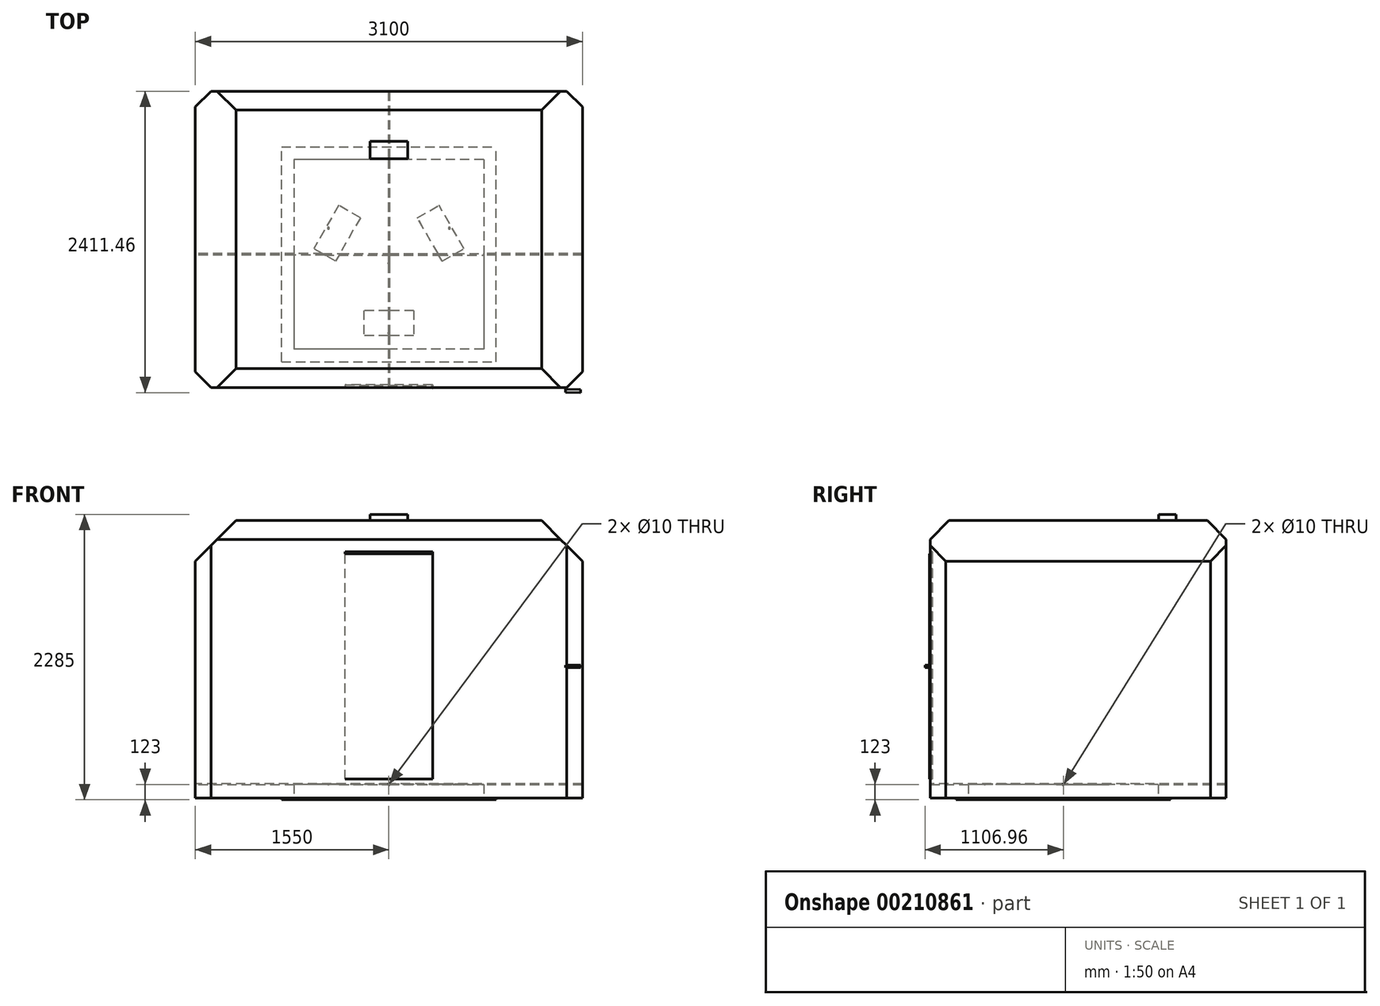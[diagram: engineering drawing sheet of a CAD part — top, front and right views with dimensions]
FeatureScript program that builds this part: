
annotation { "Feature Type Name" : "Feature", "Feature Type Description" : "" }
export const myFeature = defineFeature(function(context is Context, id is Id, definition is map)
    precondition{}
    {
        {
            var Q0;
            Q0=qCreatedBy(makeId("Front.planeOp"),FACE);
            var sketch = newSketch(context, id + "F0", { "sketchPlane" : qUnion([Q0])});
            skLineSegment(sketch, "E0.bottom", {"start": v(1550, -1110) * mm, "end": v(-1550, -1110) * mm});
            skLineSegment(sketch, "E0.top", {"start": v(1550, 1110) * mm, "end": v(-1550, 1110) * mm});
            skLineSegment(sketch, "E0.left", {"start": v(1550, -1110) * mm, "end": v(1550, 1110) * mm});
            skLineSegment(sketch, "E0.right", {"start": v(-1550, -1110) * mm, "end": v(-1550, 1110) * mm});
            skPoint(sketch, "E0.middle", {"position": v(0, 0) * mm});
            skSolve(sketch);
        }
        {
            var Q0;
            Q0=qSketchRegion(id+"F0",true);
            extrude(context, id + "F1", {"entities" : qUnion([Q0]), "depth" : 2370 * mm});
        }
        {
            var Q0;
            Q0=makeQuery(id+"F1.opExtrude","SWEPT_EDGE",EDGE,{"disambiguationData":[OSD([sQuery(id+"F0.wireOp",EDGE,"E0.top"),sQuery(id+"F0.wireOp",EDGE,"E0.right")])]});
            chamfer(context, id + "F2", {"entities" : qUnion([Q0]), "width" : 325 * mm, "tangentPropagation" : true});
        }
        {
            var Q0;
            Q0=makeQuery(id+"F1.opExtrude","SWEPT_EDGE",EDGE,{"disambiguationData":[OSD([sQuery(id+"F0.wireOp",EDGE,"E0.top"),sQuery(id+"F0.wireOp",EDGE,"E0.left")])]});
            chamfer(context, id + "F3", {"entities" : qUnion([Q0]), "width" : 325 * mm, "tangentPropagation" : true});
        }
        {
            var Q0;
            Q0=makeQuery(id+"F1.opExtrude","CAP_EDGE",EDGE,{"disambiguationData":[OSD([sQuery(id+"F0.wireOp",EDGE,"E0.left")])],"isStart":false});
            chamfer(context, id + "F4", {"entities" : qUnion([Q0]), "width" : 125 * mm, "tangentPropagation" : true});
        }
        {
            var Q0;
            Q0=makeQuery(id+"F1.opExtrude","CAP_EDGE",EDGE,{"disambiguationData":[OSD([sQuery(id+"F0.wireOp",EDGE,"E0.right")])],"isStart":false});
            chamfer(context, id + "F5", {"entities" : qUnion([Q0]), "width" : 125 * mm, "tangentPropagation" : true});
        }
        {
            var Q0;
            Q0=makeQuery(id+"F1.opExtrude","CAP_EDGE",EDGE,{"disambiguationData":[OSD([sQuery(id+"F0.wireOp",EDGE,"E0.right")])],"isStart":true});
            chamfer(context, id + "F6", {"entities" : qUnion([Q0]), "width" : 125 * mm, "tangentPropagation" : true});
        }
        {
            var Q0;
            Q0=makeQuery(id+"F1.opExtrude","CAP_EDGE",EDGE,{"disambiguationData":[OSD([sQuery(id+"F0.wireOp",EDGE,"E0.left")])],"isStart":true});
            chamfer(context, id + "F7", {"entities" : qUnion([Q0]), "width" : 125 * mm, "tangentPropagation" : true});
        }
        {
            var Q0;
            Q0=makeQuery(id+"F1.opExtrude","SWEPT_FACE",FACE,{"disambiguationData":[OSD([sQuery(id+"F0.wireOp",EDGE,"E0.bottom")])]});
            var sketch = newSketch(context, id + "F8", { "sketchPlane" : qUnion([Q0])});
            skLineSegment(sketch, "E1", {"start": v(0, 0) * mm, "end": v(0, 2370) * mm, "construction": true});
            skLineSegment(sketch, "E2", {"start": v(-1550, 1185) * mm, "end": v(1550, 1185) * mm, "construction": true});
            skLineSegment(sketch, "E3.bottom", {"start": v(759.5, 545) * mm, "end": v(-759.5, 545) * mm});
            skLineSegment(sketch, "E3.top", {"start": v(759.5, 2064) * mm, "end": v(-759.5, 2064) * mm});
            skLineSegment(sketch, "E3.left", {"start": v(759.5, 545) * mm, "end": v(759.5, 2064) * mm});
            skLineSegment(sketch, "E3.right", {"start": v(-759.5, 545) * mm, "end": v(-759.5, 2064) * mm});
            skPoint(sketch, "E3.middle", {"position": v(0, 1304.5) * mm});
            skSolve(sketch);
        }
        {
            var Q0;
            Q0=qSketchRegion(id+"F8",true);
            extrude(context, id + "F9", {"entities" : qUnion([Q0]), "operationType" : NewBodyOperationType.REMOVE, "oppositeDirection" : true, "depth" : 108 * mm});
        }
        {
            var Q0;
            Q0=makeQuery(id+"F9.boolean.opBoolean","COPY",FACE,{"derivedFrom":makeQuery(id+"F9.opExtrude","CAP_FACE",FACE,{"disambiguationData":[OSD([sQuery(id+"F8.wireOp",EDGE,"E3.bottom"),sQuery(id+"F8.wireOp",EDGE,"E3.top"),sQuery(id+"F8.wireOp",EDGE,"E3.left"),sQuery(id+"F8.wireOp",EDGE,"E3.right")])],"isStart":false})});
            var sketch = newSketch(context, id + "F10", { "sketchPlane" : qUnion([Q0])});
            skLineSegment(sketch, "E4", {"start": v(0, 2064) * mm, "end": v(0, 1375) * mm, "construction": true});
            skLineSegment(sketch, "E5.bottom", {"start": v(200, 1754) * mm, "end": v(-200, 1754) * mm});
            skLineSegment(sketch, "E5.top", {"start": v(200, 1954) * mm, "end": v(-200, 1954) * mm});
            skLineSegment(sketch, "E5.left", {"start": v(200, 1754) * mm, "end": v(200, 1954) * mm});
            skLineSegment(sketch, "E5.right", {"start": v(-200, 1754) * mm, "end": v(-200, 1954) * mm});
            skPoint(sketch, "E5.middle", {"position": v(0, 1854) * mm});
            skLineSegment(sketch, "E6", {"start": v(0, 1375) * mm, "end": v(-409.07, 1138.82) * mm, "construction": true});
            skLineSegment(sketch, "E7", {"start": v(0, 1375) * mm, "end": v(395.82, 1146.47) * mm, "construction": true});
            skCircle(sketch, "E8", {"center": v(0, 1375) * mm, "radius": 559 * mm, "construction": true});
            skCircle(sketch, "E9", {"center": v(0, 1934) * mm, "radius": 7.5 * mm});
            skCircle(sketch, "E10.MirrorC", {"center": v(484.1, 1095.5) * mm, "radius": 7.5 * mm});
            skCircle(sketch, "E11.MirrorC", {"center": v(-484.1, 1095.5) * mm, "radius": 7.5 * mm});
            skLineSegment(sketch, "E12", {"start": v(759.5, 1304.5) * mm, "end": v(-759.5, 1304.5) * mm, "construction": true});
            skLineSegment(sketch, "E13.MirrorCS", {"start": v(428.22, 1358.7) * mm, "end": v(228.22, 1012.3) * mm});
            skLineSegment(sketch, "E14.MirrorCS", {"start": v(228.22, 1012.3) * mm, "end": v(401.43, 912.3) * mm});
            skLineSegment(sketch, "E15.MirrorCS", {"start": v(601.43, 1258.7) * mm, "end": v(401.43, 912.3) * mm});
            skLineSegment(sketch, "E16.MirrorCS", {"start": v(428.22, 1358.7) * mm, "end": v(601.43, 1258.7) * mm});
            skLineSegment(sketch, "E17.MirrorCS", {"start": v(-428.22, 1358.7) * mm, "end": v(-601.43, 1258.7) * mm});
            skLineSegment(sketch, "E18.MirrorCS", {"start": v(-401.43, 912.3) * mm, "end": v(-601.43, 1258.7) * mm});
            skLineSegment(sketch, "E19.MirrorCS", {"start": v(-228.22, 1012.3) * mm, "end": v(-401.43, 912.3) * mm});
            skLineSegment(sketch, "E20.MirrorCS", {"start": v(-228.22, 1012.3) * mm, "end": v(-428.22, 1358.7) * mm});
            skCircle(sketch, "E21", {"center": v(0, 1375) * mm, "radius": 7.5 * mm});
            skSolve(sketch);
        }
        {
            var Q0;
            Q0=qSketchRegion(id+"F10",true);
            extrude(context, id + "F11", {"entities" : qUnion([Q0]), "operationType" : NewBodyOperationType.REMOVE, "oppositeDirection" : true, "depth" : 1 * mm});
        }
        {
            var Q0;
            Q0=makeQuery(id+"F9.boolean.opBoolean","COPY",FACE,{"derivedFrom":makeQuery(id+"F9.opExtrude","SWEPT_FACE",FACE,{"disambiguationData":[OSD([sQuery(id+"F8.wireOp",EDGE,"E3.right")])]})});
            var sketch = newSketch(context, id + "F12", { "sketchPlane" : qUnion([Q0])});
            skCircle(sketch, "E22", {"center": v(-1304.5, -1002) * mm, "radius": 5 * mm});
            skSolve(sketch);
        }
        {
            var Q0;
            Q0=qSketchRegion(id+"F12",true);
            extrude(context, id + "F13", {"entities" : qUnion([Q0]), "operationType" : NewBodyOperationType.REMOVE, "depth" : 1 * mm});
        }
        {
            var Q0;
            Q0=qSketchRegion(id+"F12",true);
            extrude(context, id + "F14", {"entities" : qUnion([Q0]), "operationType" : NewBodyOperationType.REMOVE, "endBound" : BoundingType.THROUGH_ALL, "oppositeDirection" : true, "depth" : 25 * mm, "hasSecondDirection" : true, "secondDirectionBound" : SecondDirectionBoundingType.THROUGH_ALL, "secondDirectionOppositeDirection" : false, "secondDirectionDepth" : 25 * mm});
        }
        {
            var Q0;
            Q0=makeQuery(id+"F9.boolean.opBoolean","COPY",FACE,{"derivedFrom":makeQuery(id+"F9.opExtrude","SWEPT_FACE",FACE,{"disambiguationData":[OSD([sQuery(id+"F8.wireOp",EDGE,"E3.bottom")])]})});
            var sketch = newSketch(context, id + "F15", { "sketchPlane" : qUnion([Q0])});
            skLineSegment(sketch, "E23", {"start": v(0, -1110) * mm, "end": v(0, -1002) * mm, "construction": true});
            skCircle(sketch, "E24", {"center": v(0, -1002) * mm, "radius": 5 * mm});
            skSolve(sketch);
        }
        {
            var Q0;
            Q0=qSketchRegion(id+"F15",true);
            extrude(context, id + "F16", {"entities" : qUnion([Q0]), "operationType" : NewBodyOperationType.REMOVE, "endBound" : BoundingType.THROUGH_ALL, "oppositeDirection" : true, "depth" : 25 * mm, "hasSecondDirection" : true, "secondDirectionBound" : SecondDirectionBoundingType.THROUGH_ALL, "secondDirectionOppositeDirection" : false, "secondDirectionDepth" : 25 * mm});
        }
        {
            var Q0;
            Q0=makeQuery(id+"F1.opExtrude","CAP_EDGE",EDGE,{"disambiguationData":[OSD([sQuery(id+"F0.wireOp",EDGE,"E0.top")])],"isStart":true});
            chamfer(context, id + "F17", {"entities" : qUnion([Q0]), "width" : 150 * mm, "tangentPropagation" : true});
        }
        {
            var Q0;
            Q0=makeQuery(id+"F1.opExtrude","CAP_EDGE",EDGE,{"disambiguationData":[OSD([sQuery(id+"F0.wireOp",EDGE,"E0.top")])],"isStart":false});
            chamfer(context, id + "F18", {"entities" : qUnion([Q0]), "width" : 150 * mm, "tangentPropagation" : true});
        }
        {
            var Q0;
            Q0=makeQuery(id+"F1.opExtrude","SWEPT_FACE",FACE,{"disambiguationData":[OSD([sQuery(id+"F0.wireOp",EDGE,"E0.bottom")])]});
            var sketch = newSketch(context, id + "F19", { "sketchPlane" : qUnion([Q0])});
            skLineSegment(sketch, "E25.bottom", {"start": v(-859.5, 2164) * mm, "end": v(859.5, 2164) * mm});
            skLineSegment(sketch, "E25.top", {"start": v(-859.5, 445) * mm, "end": v(859.5, 445) * mm});
            skLineSegment(sketch, "E25.left", {"start": v(-859.5, 2164) * mm, "end": v(-859.5, 445) * mm});
            skLineSegment(sketch, "E25.right", {"start": v(859.5, 2164) * mm, "end": v(859.5, 445) * mm});
            skLineSegment(sketch, "E26.bottom", {"start": v(-759.5, 545) * mm, "end": v(759.5, 545) * mm});
            skLineSegment(sketch, "E26.top", {"start": v(-759.5, 2064) * mm, "end": v(759.5, 2064) * mm});
            skLineSegment(sketch, "E26.left", {"start": v(-759.5, 545) * mm, "end": v(-759.5, 2064) * mm});
            skLineSegment(sketch, "E26.right", {"start": v(759.5, 545) * mm, "end": v(759.5, 2064) * mm});
            skSolve(sketch);
        }
        {
            var Q0;
            Q0=qSketchRegion(id+"F19",true);
            extrude(context, id + "F20", {"entities" : qUnion([Q0]), "operationType" : NewBodyOperationType.ADD, "depth" : 15 * mm});
        }
        {
            var Q0;
            Q0=makeQuery(id+"F1.opExtrude","CAP_FACE",FACE,{"disambiguationData":[OSD([sQuery(id+"F0.wireOp",EDGE,"E0.bottom"),sQuery(id+"F0.wireOp",EDGE,"E0.top"),sQuery(id+"F0.wireOp",EDGE,"E0.left"),sQuery(id+"F0.wireOp",EDGE,"E0.right")])],"isStart":false});
            var sketch = newSketch(context, id + "F21", { "sketchPlane" : qUnion([Q0])});
            skLineSegment(sketch, "E27", {"start": v(0, 960) * mm, "end": v(0, -367.55) * mm, "construction": true});
            skPoint(sketch, "E28.middle", {"position": v(0, -75) * mm});
            skPoint(sketch, "E29.middle", {"position": v(0, -1025) * mm});
            skLineSegment(sketch, "E30.bottom", {"start": v(350, -960) * mm, "end": v(-350, -960) * mm});
            skLineSegment(sketch, "E30.top", {"start": v(350, 860) * mm, "end": v(-350, 860) * mm});
            skLineSegment(sketch, "E30.left", {"start": v(350, -960) * mm, "end": v(350, 860) * mm});
            skLineSegment(sketch, "E30.right", {"start": v(-350, -960) * mm, "end": v(-350, 860) * mm});
            skPoint(sketch, "E30.middle", {"position": v(0, -50) * mm});
            skSolve(sketch);
        }
        {
            var Q0;
            Q0=qSketchRegion(id+"F21",true);
            extrude(context, id + "F22", {"entities" : qUnion([Q0]), "operationType" : NewBodyOperationType.REMOVE, "oppositeDirection" : true, "depth" : 20 * mm});
        }
        {
            var Q0;
            Q0=makeQuery(id+"F1.opExtrude","SWEPT_FACE",FACE,{"disambiguationData":[OSD([sQuery(id+"F0.wireOp",EDGE,"E0.top")])]});
            var sketch = newSketch(context, id + "F23", { "sketchPlane" : qUnion([Q0])});
            skLineSegment(sketch, "E31", {"start": v(0, -150) * mm, "end": v(0, -1860.94) * mm, "construction": true});
            skPoint(sketch, "E31.endSnap0", {"position": v(0, -150) * mm});
            skLineSegment(sketch, "E32.bottom", {"start": v(150, -540) * mm, "end": v(-150, -540) * mm});
            skLineSegment(sketch, "E32.top", {"start": v(150, -400) * mm, "end": v(-150, -400) * mm});
            skLineSegment(sketch, "E32.left", {"start": v(150, -540) * mm, "end": v(150, -400) * mm});
            skLineSegment(sketch, "E32.right", {"start": v(-150, -540) * mm, "end": v(-150, -400) * mm});
            skPoint(sketch, "E32.middle", {"position": v(0, -470) * mm});
            skSolve(sketch);
        }
        {
            var Q0;
            Q0=qSketchRegion(id+"F23",true);
            extrude(context, id + "F24", {"entities" : qUnion([Q0]), "operationType" : NewBodyOperationType.ADD, "depth" : 50 * mm});
        }
        {
            var Q0;
            Q0=makeQuery(id+"F22.boolean.opBoolean","COPY",FACE,{"derivedFrom":makeQuery(id+"F22.opExtrude","SWEPT_FACE",FACE,{"disambiguationData":[OSD([sQuery(id+"F21.wireOp",EDGE,"E30.bottom")])]})});
            var sketch = newSketch(context, id + "F25", { "sketchPlane" : qUnion([Q0])});
            skLineSegment(sketch, "E33.bottom", {"start": v(-350.17, -2370) * mm, "end": v(349.8, -2376.1) * mm});
            skLineSegment(sketch, "E33.top", {"start": v(-350, -2350) * mm, "end": v(349.97, -2356.1) * mm});
            skLineSegment(sketch, "E33.left", {"start": v(-350.17, -2370) * mm, "end": v(-350, -2350) * mm});
            skLineSegment(sketch, "E33.right", {"start": v(349.8, -2376.1) * mm, "end": v(349.97, -2356.1) * mm});
            skSolve(sketch);
        }
        {
            var Q0;
            Q0=qSketchRegion(id+"F25",true);
            extrude(context, id + "F26", {"entities" : qUnion([Q0]), "operationType" : NewBodyOperationType.ADD, "depth" : 1805 * mm});
        }
        {
            var Q0;
            Q0=makeQuery(id+"F26.opExtrude","SWEPT_FACE",FACE,{"disambiguationData":[OSD([sQuery(id+"F25.wireOp",EDGE,"E33.bottom")])]});
            var sketch = newSketch(context, id + "F27", { "sketchPlane" : qUnion([Q0])});
            skLineSegment(sketch, "E34.bottom", {"start": v(1436.7, -67.5) * mm, "end": v(1556.7, -67.5) * mm});
            skLineSegment(sketch, "E34.top", {"start": v(1436.7, -47.5) * mm, "end": v(1556.7, -47.5) * mm});
            skLineSegment(sketch, "E34.left", {"start": v(1436.7, -67.5) * mm, "end": v(1436.7, -47.5) * mm});
            skLineSegment(sketch, "E34.right", {"start": v(1556.7, -67.5) * mm, "end": v(1556.7, -47.5) * mm});
            skPoint(sketch, "E34.middle", {"position": v(1496.7, -57.5) * mm});
            skPoint(sketch, "E34.middle.positionSnap0", {"position": v(370.52, -57.5) * mm});
            skPoint(sketch, "E34.centerSnap0", {"position": v(370.52, -57.5) * mm});
            skSolve(sketch);
        }
        {
            var Q0;
            Q0=qSketchRegion(id+"F27",true);
            extrude(context, id + "F28", {"entities" : qUnion([Q0]), "operationType" : NewBodyOperationType.ADD, "depth" : 25 * mm});
        }
    });
